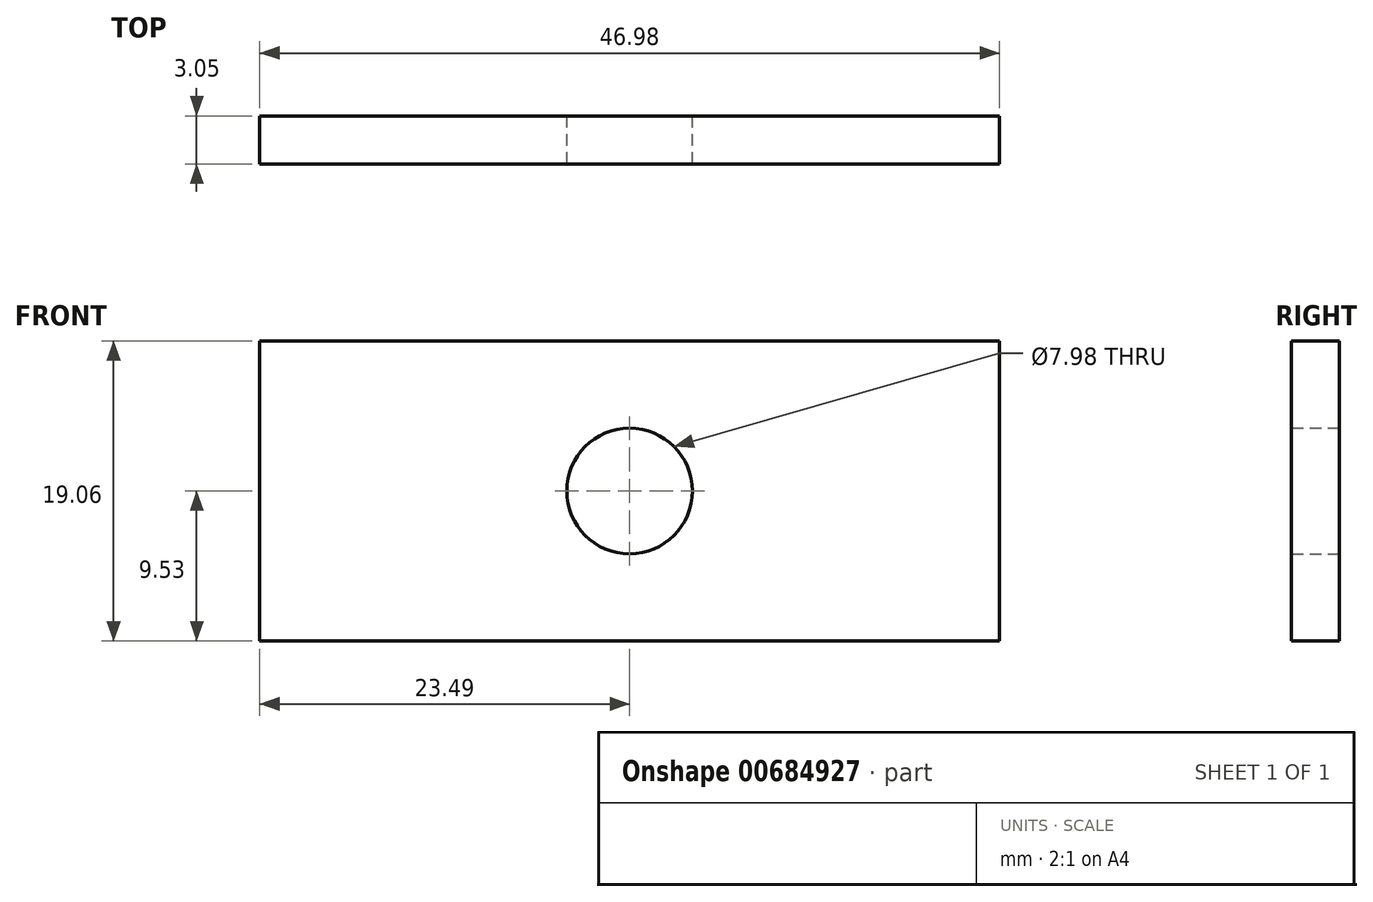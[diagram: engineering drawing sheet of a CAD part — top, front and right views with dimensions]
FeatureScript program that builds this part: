
annotation { "Feature Type Name" : "Feature", "Feature Type Description" : "" }
export const myFeature = defineFeature(function(context is Context, id is Id, definition is map)
    precondition{}
    {
        {
            var Q0;
            Q0=qCreatedBy(makeId("Front.planeOp"),FACE);
            var sketch = newSketch(context, id + "F0", { "sketchPlane" : qUnion([Q0])});
            skLineSegment(sketch, "E0.bottom", {"start": v(23.5, 9.52) * mm, "end": v(-23.5, 9.52) * mm});
            skLineSegment(sketch, "E0.top", {"start": v(23.5, -9.53) * mm, "end": v(-23.5, -9.53) * mm});
            skLineSegment(sketch, "E0.left", {"start": v(23.5, 9.52) * mm, "end": v(23.5, -9.53) * mm});
            skLineSegment(sketch, "E0.right", {"start": v(-23.5, 9.52) * mm, "end": v(-23.5, -9.53) * mm});
            skPoint(sketch, "E0.middle", {"position": v(0, 0) * mm});
            skCircle(sketch, "E1", {"center": v(0, 0) * mm, "radius": 3.99 * mm});
            skSolve(sketch);
        }
        {
            var Q0;
            Q0 = qSketchRegion(id + "F0", true);
            extrude(context, id + "F1", {"entities" : qUnion([Q0]), "depth" : 3.05 * mm, "offsetDistance" : 25.4 * mm});
        }
    });
